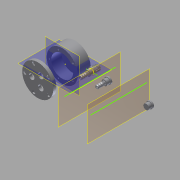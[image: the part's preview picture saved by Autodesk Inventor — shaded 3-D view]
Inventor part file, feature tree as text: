
AUTODESK INVENTOR PART (.ipt)
format: ipt  version: 2012 (Build 160160000, 160)  size: 578,560 bytes
history: native  units: in
note: dims shown in document units (in); Inventor stores cm internally (conversion verified against a paired STEP export)
features: sketch x18, extrude x14, plane x4, revolve x2, mirror x2
ambient origin geometry x8: Origin, YZ Plane, XZ Plane, XY Plane, X Axis, Y Axis, Z Axis, Center Point
bodies: Solid1 (feature_tree)
feature tree (40):
  extrude  "Extrusion1"  Depth=0.3in TaperAngle=0.0deg
  extrude  "Extrusion2"  Depth=0.1135in TaperAngle=0.0deg
  extrude  "Extrusion3"  Depth=0.158in
  plane  "Work Plane1"
  extrude  "Extrusion4"  Depth=0.4in TaperAngle=0.0deg
  extrude  "Extrusion5"  Depth=2.125in
  extrude  "Extrusion6"  Depth=0.25in TaperAngle=0.0deg
  extrude  "Extrusion7"  Depth=0.586in
  sketch  "Sketch8"  dims[d28=1.1811in d30=360.0deg d32=0.4in d33=0.0in]
  plane  "Work Plane2"
  revolve  "Revolution1"  [1 undecoded]
  extrude  "Extrusion8"  Depth=0.53in
  extrude  "Extrusion9"  Depth=0.3in TaperAngle=0.0deg
  revolve  "Revolution2"  [1 undecoded]
  sketch  "Sketch14"  dims[d50=15.0deg d51=0.055in]
  plane  "Work Plane3"
  plane  "Work Plane4"
  mirror  "Mirror1"
  extrude  "Extrusion10"  TaperAngle=90.0deg  [1 undecoded]
  mirror  "Mirror2"
  extrude  "Extrusion11"  Depth=0.055in
  extrude  "Extrusion12"  Depth=0.055in
  extrude  "Extrusion13"  Depth=0.055in
  extrude  "Extrusion14"  Depth=0.055in
  sketch  "Sketch1"  dims[d0=3.0in d1=0.3in d2=0.0in]
  sketch  "Sketch2"  dims[d6=1.9685in d8=360.0deg d10=0.1135in d11=0.0in]
  sketch  "Sketch3"  dims[d12=1.25in d13=0.158in]
  sketch  "Sketch4"  dims[d14=1.9685in d16=360.0deg d18=0.4in d19=0.0in]
  sketch  "Sketch5"  dims[d20=2.0625in d21=2.125in]
  sketch  "Sketch6"  dims[d22=1.0in d23=0.0in d24=0.25in d25=0.0in]
  sketch  "Sketch7"  dims[d26=0.53in d27=0.586in]
  sketch  "Sketch9"  dims[d34=0.53in d35=0.53in]
  sketch  "Sketch10"  dims[d36=0.23in d37=0.3in d38=0.0in]
  sketch  "Sketch11"  dims[d39=90.0deg d43=0.0in]
  sketch  "Sketch13"  dims[d46=0.15in d49=90.0deg]
  sketch  "Sketch15"  dims[d52=15.0deg d53=0.055in]
  sketch  "Sketch16"  dims[d54=15.0deg d55=0.055in]
  sketch  "Sketch17"  dims[d56=0.055in d57=0.055in]
  sketch  "Sketch18"  dims[d58=0.25in]
  sketch  "Sketch19"  dims[d59=1.0in d60=0.0in d61=0.635in d62=0.15in d63=0.0in d64=0.15in d65=0.18in d66=90.0deg d67=90.0deg d68=90.0deg d69=1.0in d70=0.0in d71=1.0in d72=0.0in d73=0.45in d74=0.0in d75=3.0in d76=0.0in d77=0.0177in d78=0.0in]
note: 3 required parameter values undecoded (feature->parameter linkage not recoverable at this tier; creation-order binding heuristic only, values carry confidence <= 0.55)